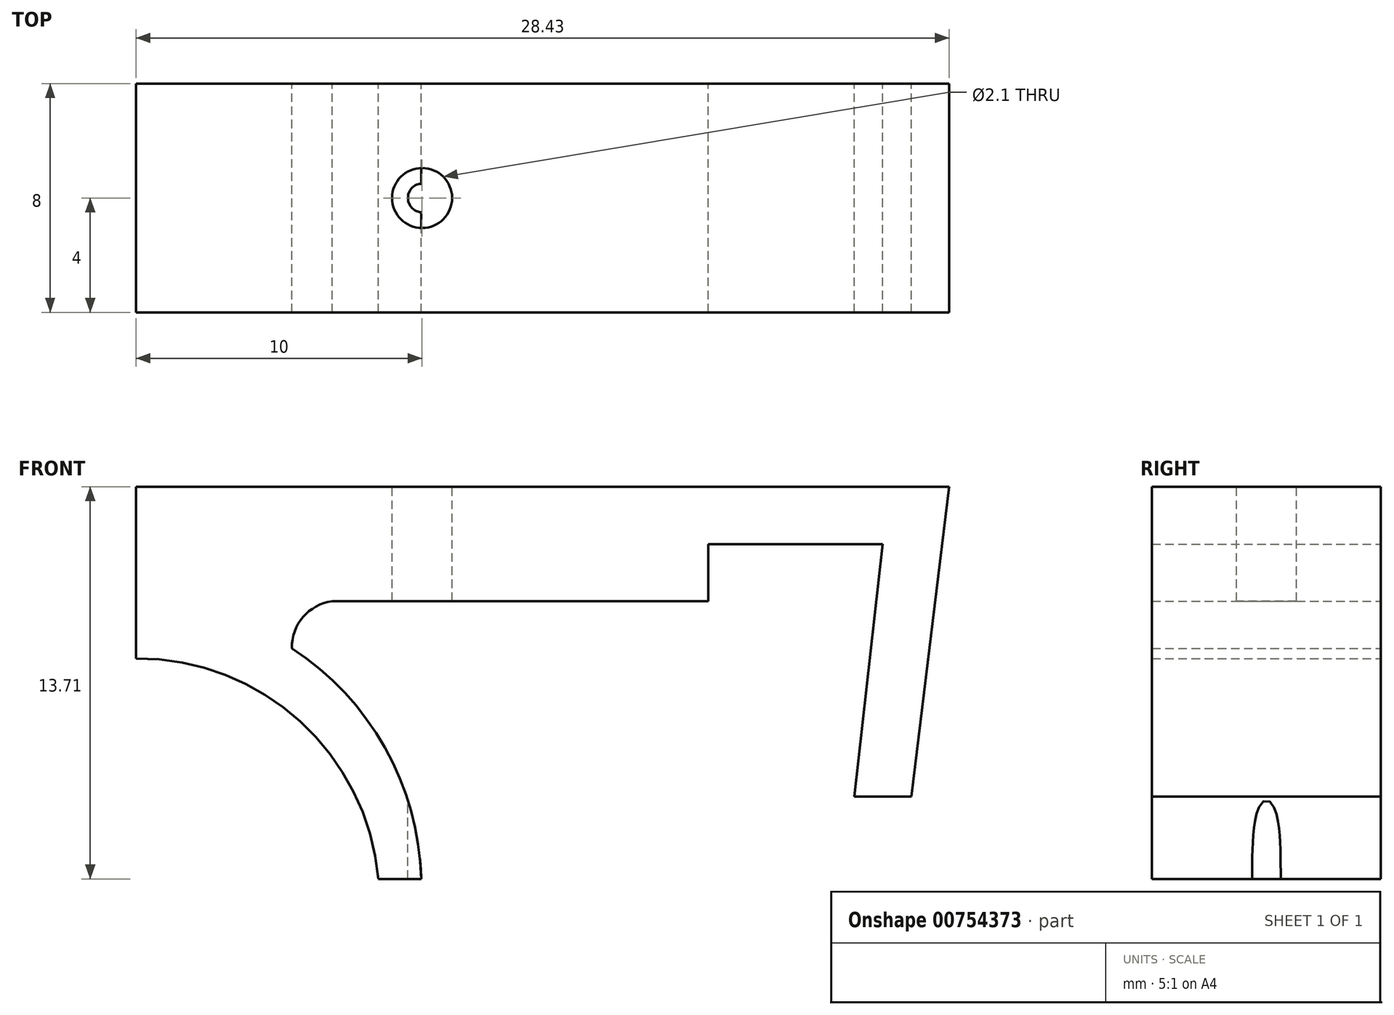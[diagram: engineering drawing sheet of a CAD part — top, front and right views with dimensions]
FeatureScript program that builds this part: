
annotation { "Feature Type Name" : "Feature", "Feature Type Description" : "" }
export const myFeature = defineFeature(function(context is Context, id is Id, definition is map)
    precondition{}
    {
        {
            var Q0;
            Q0=qCreatedBy(makeId("Front.planeOp"),FACE);
            var sketch = newSketch(context, id + "F0", { "sketchPlane" : qUnion([Q0])});
            skLineSegment(sketch, "E0.bottom", {"start": v(-10, -5) * mm, "end": v(10, -5) * mm});
            skLineSegment(sketch, "E0.top", {"start": v(-10, 5) * mm, "end": v(10, 5) * mm});
            skLineSegment(sketch, "E0.left", {"start": v(-10, -5) * mm, "end": v(-10, 5) * mm});
            skLineSegment(sketch, "E0.right", {"start": v(10, -5) * mm, "end": v(10, 5) * mm});
            skPoint(sketch, "E0.middle", {"position": v(0, 0) * mm});
            skPoint(sketch, "E1", {"position": v(-10, -15) * mm});
            skArc(sketch, "E2", {"start": v(-0.03, -14.71) * mm, "mid": v(-1.3, -10.12) * mm, "end": v(-4.55, -6.65) * mm});
            skLineSegment(sketch, "E3", {"start": v(-10, -5) * mm, "end": v(-10, -7) * mm});
            skLineSegment(sketch, "E4", {"start": v(-0.03, -14.71) * mm, "end": v(-1.53, -14.71) * mm});
            skArc(sketch, "E5", {"start": v(-1.53, -14.71) * mm, "mid": v(-4.26, -9.2) * mm, "end": v(-10, -7) * mm});
            skArc(sketch, "E6", {"start": v(-3.14, -5) * mm, "mid": v(-4.16, -5.55) * mm, "end": v(-4.55, -6.65) * mm});
            skArc(sketch, "E7.MirrorCS", {"start": v(0.03, -14.71) * mm, "mid": v(1.3, -10.12) * mm, "end": v(4.55, -6.65) * mm});
            skArc(sketch, "E8.MirrorCS", {"start": v(1.53, -14.71) * mm, "mid": v(4.26, -9.2) * mm, "end": v(10, -7) * mm});
            skLineSegment(sketch, "E9.MirrorCS", {"start": v(0.03, -14.71) * mm, "end": v(1.53, -14.71) * mm});
            skArc(sketch, "E10.MirrorCS", {"start": v(3.14, -5) * mm, "mid": v(4.16, -5.55) * mm, "end": v(4.55, -6.65) * mm});
            skLineSegment(sketch, "E11.MirrorCS", {"start": v(10, -5) * mm, "end": v(10, -7) * mm});
            skSolve(sketch);
        }
        {
            var Q0;
            Q0=makeQuery(id+"F0.imprint","IMPRINT",FACE,{"disambiguationData":[TD([[makeQuery(id+"F0.imprint","IMPRINT",EDGE,{"derivedFrom":sQuery(id+"F0.wireOp",EDGE,"E0.top")}),-1.0]])]});
            var Q1;
            Q1=makeQuery(id+"F0.imprint","IMPRINT",FACE,{"disambiguationData":[TD([[makeQuery(id+"F0.imprint","IMPRINT",EDGE,{"derivedFrom":sQuery(id+"F0.wireOp",EDGE,"E7.MirrorCS")}),-1.0]])]});
            var Q2;
            Q2=makeQuery(id+"F0.imprint","IMPRINT",FACE,{"disambiguationData":[TD([[makeQuery(id+"F0.imprint","IMPRINT",EDGE,{"derivedFrom":sQuery(id+"F0.wireOp",EDGE,"E2")}),1.0]])]});
            extrude(context, id + "F1", {"entities" : qUnion([Q0, Q1, Q2]), "endBound" : BoundingType.SYMMETRIC, "depth" : 8 * mm, "offsetDistance" : 25 * mm});
        }
        {
            var Q0;
            Q0=makeQuery(id+"F1.opExtrude","SWEPT_FACE",FACE,{"disambiguationData":[OSD([sQuery(id+"F0.wireOp",EDGE,"E0.top")])]});
            var sketch = newSketch(context, id + "F2", { "sketchPlane" : qUnion([Q0])});
            skCircle(sketch, "E12", {"center": v(0, 0) * mm, "radius": 1.05 * mm});
            skCircle(sketch, "E13", {"center": v(0, 0) * mm, "radius": 0.5 * mm});
            skSolve(sketch);
        }
        {
            var Q0;
            Q0=makeQuery(id+"F2.imprint","IMPRINT",FACE,{"disambiguationData":[TD([[makeQuery(id+"F2.imprint","IMPRINT",EDGE,{"derivedFrom":sQuery(id+"F2.wireOp",EDGE,"E13")}),1.0]])]});
            extrude(context, id + "F3", {"entities" : qUnion([Q0]), "operationType" : NewBodyOperationType.REMOVE, "oppositeDirection" : true, "depth" : 25 * mm, "offsetDistance" : 25 * mm});
        }
        {
            var Q0;
            Q0=makeQuery(id+"F2.imprint","IMPRINT",FACE,{"disambiguationData":[TD([[makeQuery(id+"F2.imprint","IMPRINT",EDGE,{"derivedFrom":sQuery(id+"F2.wireOp",EDGE,"E12")}),1.0]])]});
            extrude(context, id + "F4", {"entities" : qUnion([Q0]), "operationType" : NewBodyOperationType.REMOVE, "oppositeDirection" : true, "depth" : 10 * mm, "offsetDistance" : 25 * mm});
        }
        {
            var Q0;
            Q0=makeQuery(id+"F2.imprint","IMPRINT",FACE,{"disambiguationData":[TD([[makeQuery(id+"F2.imprint","IMPRINT",EDGE,{"derivedFrom":sQuery(id+"F2.wireOp",EDGE,"E12")}),-1.0]])]});
            extrude(context, id + "F5", {"entities" : qUnion([Q0]), "operationType" : NewBodyOperationType.REMOVE, "oppositeDirection" : true, "depth" : 6 * mm, "offsetDistance" : 25 * mm});
        }
        {
            var Q0;
            Q0=makeQuery(id+"F1.opExtrude","SWEPT_FACE",FACE,{"disambiguationData":[OSD([sQuery(id+"F0.wireOp",EDGE,"E0.right"),sQuery(id+"F0.wireOp",EDGE,"E11.MirrorCS")])]});
            var sketch = newSketch(context, id + "F6", { "sketchPlane" : qUnion([Q0])});
            skLineSegment(sketch, "E14.0", {"start": v(-4, -7) * mm, "end": v(-4, -1) * mm});
            skLineSegment(sketch, "E14.1", {"start": v(-4, -1) * mm, "end": v(4, -1) * mm});
            skLineSegment(sketch, "E14.2", {"start": v(4, -7) * mm, "end": v(4, -1) * mm});
            skLineSegment(sketch, "E15", {"start": v(-4, -3) * mm, "end": v(4, -3) * mm});
            skSolve(sketch);
        }
        {
            var Q0;
            {var subQ0=sQuery(id+"F6.wireOp",EDGE,"E14.1");Q0=makeQuery(id+"F6.imprint","IMPRINT",FACE,{"disambiguationData":[TD([[makeQuery(id+"F6.imprint","IMPRINT",EDGE,{"derivedFrom":subQ0}),-1.0]])]});}
            extrude(context, id + "F7", {"entities" : qUnion([Q0]), "operationType" : NewBodyOperationType.ADD, "depth" : 6.1 * mm, "offsetDistance" : 25 * mm});
        }
        {
            var Q0;
            Q0=makeQuery(id+"F7.boolean.opBoolean","MERGE",FACE,{"derivedFrom":[makeQuery(id+"F1.opExtrude","CAP_FACE",FACE,{"disambiguationData":[OSD([sQuery(id+"F0.wireOp",EDGE,"E0.bottom"),sQuery(id+"F0.wireOp",EDGE,"E0.top"),sQuery(id+"F0.wireOp",EDGE,"E0.left"),sQuery(id+"F0.wireOp",EDGE,"E0.right"),sQuery(id+"F0.wireOp",EDGE,"E2"),sQuery(id+"F0.wireOp",EDGE,"E3"),sQuery(id+"F0.wireOp",EDGE,"E4"),sQuery(id+"F0.wireOp",EDGE,"E5"),sQuery(id+"F0.wireOp",EDGE,"E6"),sQuery(id+"F0.wireOp",EDGE,"E7.MirrorCS"),sQuery(id+"F0.wireOp",EDGE,"E8.MirrorCS"),sQuery(id+"F0.wireOp",EDGE,"E9.MirrorCS"),sQuery(id+"F0.wireOp",EDGE,"E10.MirrorCS"),sQuery(id+"F0.wireOp",EDGE,"E11.MirrorCS")])],"isStart":true}),makeQuery(id+"F7.opExtrude","SWEPT_FACE",FACE,{"disambiguationData":[OSD([sQuery(id+"F6.wireOp",EDGE,"E14.2")])]})]});
            var sketch = newSketch(context, id + "F8", { "sketchPlane" : qUnion([Q0])});
            skLineSegment(sketch, "E16.0", {"start": v(-16.1, -3) * mm, "end": v(-16.1, -1) * mm});
            skLineSegment(sketch, "E16.1", {"start": v(-16.1, -3) * mm, "end": v(-10, -3) * mm});
            skLineSegment(sketch, "E16.2", {"start": v(-10, -7) * mm, "end": v(-10, -3) * mm});
            skLineSegment(sketch, "E17", {"start": v(-16.1, -3) * mm, "end": v(-15.1, -11.83) * mm});
            skLineSegment(sketch, "E18", {"start": v(-15.1, -11.83) * mm, "end": v(-17.1, -11.83) * mm});
            skLineSegment(sketch, "E19", {"start": v(-17.1, -11.83) * mm, "end": v(-18.43, -1) * mm});
            skLineSegment(sketch, "E20", {"start": v(-18.43, -1) * mm, "end": v(-16.1, -1) * mm});
            skSolve(sketch);
        }
        {
            var Q0;
            Q0=makeQuery(id+"F8.imprint","IMPRINT",FACE,{"disambiguationData":[TD([[makeQuery(id+"F8.imprint","IMPRINT",EDGE,{"derivedFrom":sQuery(id+"F8.wireOp",EDGE,"E16.0")}),1.0]])]});
            extrude(context, id + "F9", {"entities" : qUnion([Q0]), "operationType" : NewBodyOperationType.ADD, "oppositeDirection" : true, "depth" : 8 * mm, "offsetDistance" : 25 * mm});
        }
    });
